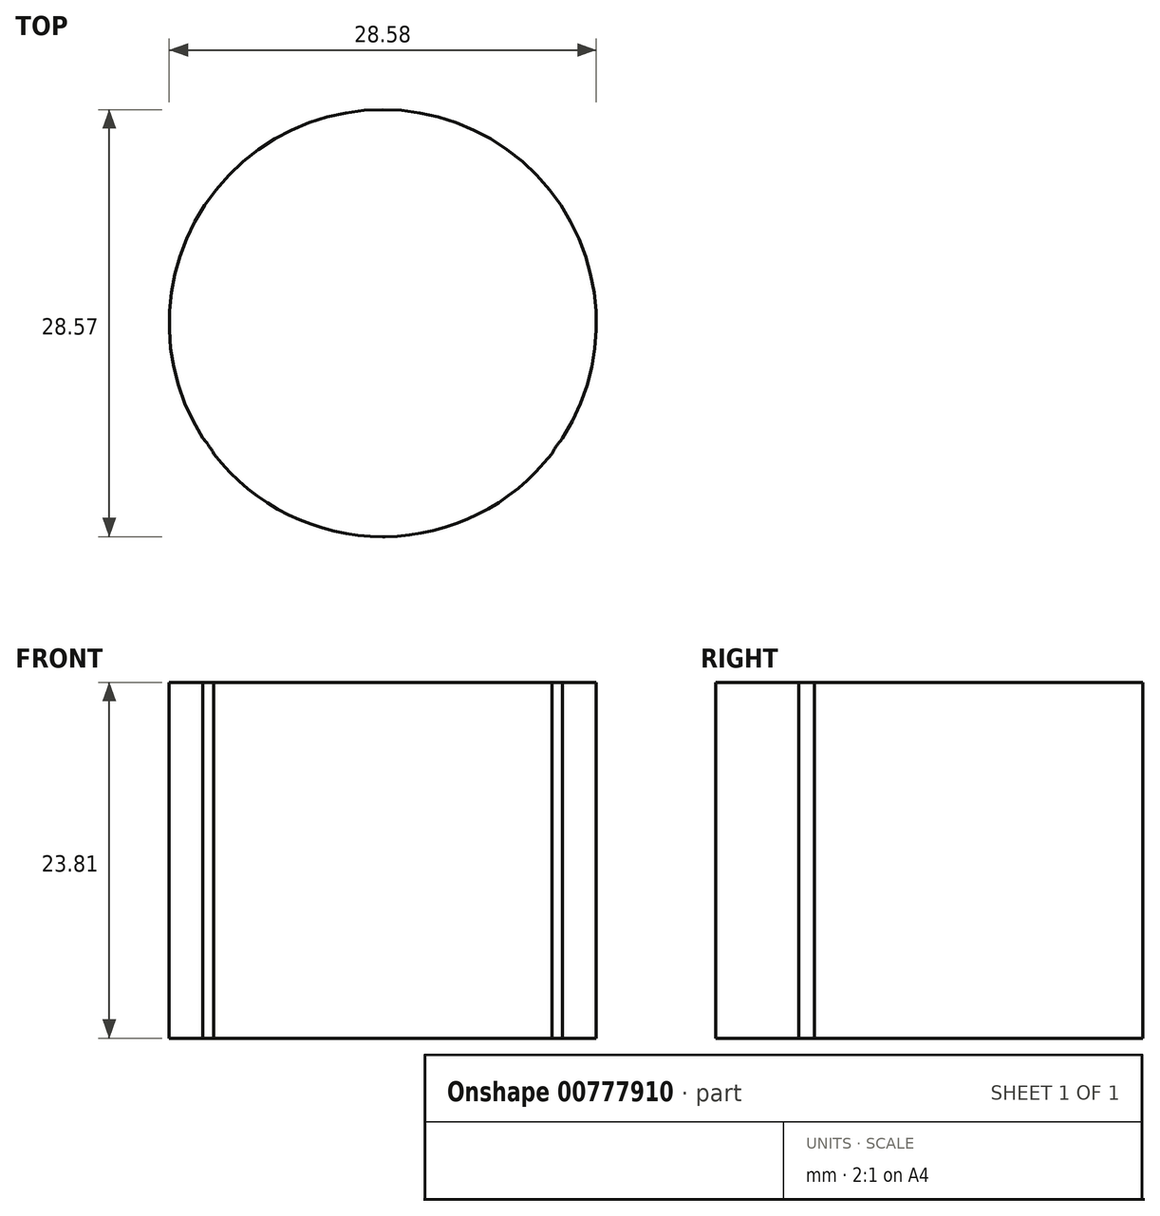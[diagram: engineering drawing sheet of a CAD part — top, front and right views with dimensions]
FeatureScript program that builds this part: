
annotation { "Feature Type Name" : "Feature", "Feature Type Description" : "" }
export const myFeature = defineFeature(function(context is Context, id is Id, definition is map)
    precondition{}
    {
        {
            var Q0;
            Q0=qCreatedBy(makeId("Top.planeOp"),FACE);
            var sketch = newSketch(context, id + "F0", { "sketchPlane" : qUnion([Q0])});
            skCircle(sketch, "E0", {"center": v(0, 0) * mm, "radius": 33.34 * mm});
            skLineSegment(sketch, "E1", {"start": v(0, 33.34) * mm, "end": v(0, 115.89) * mm});
            skLineSegment(sketch, "E2", {"start": v(0, 115.89) * mm, "end": v(0, 144.46) * mm});
            skLineSegment(sketch, "E3", {"start": v(0, 115.89) * mm, "end": v(0, 130.18) * mm});
            skCircle(sketch, "E4", {"center": v(0, 130.18) * mm, "radius": 14.29 * mm});
            skLineSegment(sketch, "E5", {"start": v(0, 115.89) * mm, "end": v(0, 109.54) * mm});
            skLineSegment(sketch, "E6", {"start": v(0, 109.54) * mm, "end": v(8.73, 109.54) * mm});
            skLineSegment(sketch, "E7", {"start": v(8.73, 109.54) * mm, "end": v(0, 109.54) * mm});
            skLineSegment(sketch, "E8", {"start": v(0, 109.54) * mm, "end": v(-8.73, 109.54) * mm});
            skFitSpline(sketch, "E9", {"points": [v(8.73, 109.54) * mm, v(9.35, 115.94) * mm, v(11.31, 121.45) * mm, v(12.03, 122.47) * mm], "startDerivative": vector(0.44, 14.94) * mm, "endDerivative": vector(3.59, 4.17) * mm});
            skLineSegment(sketch, "E10", {"start": v(8.8, 111.62) * mm, "end": v(0, 111.62) * mm});
            skLineSegment(sketch, "E11", {"start": v(0, 111.62) * mm, "end": v(-8.79, 111.62) * mm});
            skLineSegment(sketch, "E12", {"start": v(9.35, 115.94) * mm, "end": v(0, 115.89) * mm});
            skLineSegment(sketch, "E13", {"start": v(-9.35, 115.89) * mm, "end": v(0, 115.89) * mm});
            skLineSegment(sketch, "E14", {"start": v(11.31, 121.45) * mm, "end": v(0, 121.45) * mm});
            skLineSegment(sketch, "E15", {"start": v(0, 121.45) * mm, "end": v(-11.31, 121.45) * mm});
            skLineSegment(sketch, "E16", {"start": v(12.03, 122.47) * mm, "end": v(0, 122.47) * mm});
            skLineSegment(sketch, "E17", {"start": v(0, 122.47) * mm, "end": v(-12.03, 122.47) * mm});
            skFitSpline(sketch, "E18", {"points": [v(-8.79, 111.62) * mm, v(-9.35, 115.89) * mm, v(-11.31, 121.45) * mm, v(-12.03, 122.47) * mm], "startDerivative": vector(-0.67, 10.56) * mm, "endDerivative": vector(-3.31, 3.73) * mm});
            skFitSpline(sketch, "E19", {"points": [v(-8.73, 109.54) * mm, v(-8.79, 111.62) * mm], "startDerivative": vector(-0.06, 2.08) * mm, "endDerivative": vector(-0.06, 2.08) * mm});
            skLineSegment(sketch, "E20", {"start": v(0, 33.34) * mm, "end": v(0, 63.5) * mm});
            skLineSegment(sketch, "E21", {"start": v(0, 63.5) * mm, "end": v(9.52, 63.5) * mm});
            skLineSegment(sketch, "E22", {"start": v(0, 63.5) * mm, "end": v(-9.53, 63.5) * mm});
            skFitSpline(sketch, "E23", {"points": [v(9.52, 63.5) * mm, v(8.73, 109.54) * mm], "startDerivative": vector(-0.8, 39.69) * mm, "endDerivative": vector(-0.8, 39.69) * mm});
            skFitSpline(sketch, "E24", {"points": [v(-9.53, 63.5) * mm, v(-8.75, 110.23) * mm], "startDerivative": vector(0.78, 40.38) * mm, "endDerivative": vector(0.78, 40.38) * mm});
            skLineSegment(sketch, "E25", {"start": v(0, 33.34) * mm, "end": v(0, 57.15) * mm});
            skLineSegment(sketch, "E26", {"start": v(0, 57.15) * mm, "end": v(11.11, 57.15) * mm});
            skLineSegment(sketch, "E27", {"start": v(0, 57.15) * mm, "end": v(-11.11, 57.15) * mm});
            skLineSegment(sketch, "E28", {"start": v(0, 33.34) * mm, "end": v(0, 49.21) * mm});
            skLineSegment(sketch, "E29", {"start": v(0, 49.21) * mm, "end": v(14.29, 49.21) * mm});
            skLineSegment(sketch, "E30", {"start": v(0, 49.21) * mm, "end": v(-14.29, 49.21) * mm});
            skCircle(sketch, "E31", {"center": v(0, 0) * mm, "radius": 30.96 * mm});
            skLineSegment(sketch, "E32", {"start": v(0, 33.34) * mm, "end": v(0, 42.86) * mm});
            skLineSegment(sketch, "E33", {"start": v(0, 42.86) * mm, "end": v(0, 33.34) * mm});
            skLineSegment(sketch, "E34", {"start": v(0, 42.86) * mm, "end": v(16.67, 42.86) * mm});
            skLineSegment(sketch, "E35", {"start": v(0, 42.86) * mm, "end": v(-16.66, 42.86) * mm});
            skLineSegment(sketch, "E36", {"start": v(0, 33.34) * mm, "end": v(0, 0) * mm});
            skLineSegment(sketch, "E37", {"start": v(0, 0) * mm, "end": v(33.34, 0) * mm});
            skLineSegment(sketch, "E38", {"start": v(33.34, 0) * mm, "end": v(33.34, 25.4) * mm});
            skLineSegment(sketch, "E39", {"start": v(33.34, 25.4) * mm, "end": v(-21.6, 25.4) * mm});
            skLineSegment(sketch, "E40", {"start": v(33.34, 25.4) * mm, "end": v(21.6, 25.4) * mm});
            skFitSpline(sketch, "E41", {"points": [v(9.52, 63.5) * mm, v(11.11, 57.15) * mm, v(14.29, 49.21) * mm, v(16.67, 42.86) * mm, v(20.38, 33.37) * mm, v(21.6, 25.4) * mm], "startDerivative": vector(6.83, -33.8) * mm, "endDerivative": vector(3.07, -38.36) * mm});
            skLineSegment(sketch, "E42", {"start": v(0, 33.34) * mm, "end": v(-20.37, 33.34) * mm});
            skFitSpline(sketch, "E43", {"points": [v(-9.53, 63.5) * mm, v(-11.11, 57.15) * mm, v(-14.29, 49.21) * mm, v(-16.66, 42.86) * mm, v(-20.37, 33.34) * mm, v(-21.6, 25.4) * mm], "startDerivative": vector(-6.82, -33.8) * mm, "endDerivative": vector(-3.13, -38.24) * mm});
            skLineSegment(sketch, "E44", {"start": v(21.6, 25.4) * mm, "end": v(39.69, 25.4) * mm});
            skLineSegment(sketch, "E45", {"start": v(39.69, 25.4) * mm, "end": v(39.69, 0) * mm});
            skLineSegment(sketch, "E46", {"start": v(39.69, 0) * mm, "end": v(33.34, 0) * mm});
            skLineSegment(sketch, "E47", {"start": v(-21.6, 25.4) * mm, "end": v(-39.69, 25.4) * mm});
            skLineSegment(sketch, "E48", {"start": v(-39.69, 25.4) * mm, "end": v(-39.69, 0) * mm});
            skLineSegment(sketch, "E49", {"start": v(-39.69, 0) * mm, "end": v(-33.34, 0) * mm});
            skSolve(sketch);
        }
        {
            var Q0;
            {var subQ0=sQuery(id+"F0.wireOp",EDGE,"E2");Q0=makeQuery(id+"F0.imprint","IMPRINT",FACE,{"disambiguationData":[TD([[makeQuery(id+"F0.imprint","IMPRINT",EDGE,{"derivedFrom":subQ0}),1.0]])]});}
            var Q1;
            {var subQ0=sQuery(id+"F0.wireOp",EDGE,"E2");Q1=makeQuery(id+"F0.imprint","IMPRINT",FACE,{"disambiguationData":[TD([[makeQuery(id+"F0.imprint","IMPRINT",EDGE,{"derivedFrom":subQ0}),-1.0]])]});}
            var Q2;
            {var subQ0=sQuery(id+"F0.wireOp",EDGE,"E14");Q2=makeQuery(id+"F0.imprint","IMPRINT",FACE,{"disambiguationData":[TD([[makeQuery(id+"F0.imprint","IMPRINT",EDGE,{"derivedFrom":subQ0}),-1.0]])]});}
            var Q3;
            {var subQ3=sQuery(id+"F0.wireOp",EDGE,"E14");Q3=makeQuery(id+"F0.imprint","IMPRINT",FACE,{"disambiguationData":[TD([[makeQuery(id+"F0.imprint","IMPRINT",EDGE,{"derivedFrom":subQ3}),1.0]])]});}
            var Q4;
            {var subQ0=sQuery(id+"F0.wireOp",EDGE,"E15");Q4=makeQuery(id+"F0.imprint","IMPRINT",FACE,{"disambiguationData":[TD([[makeQuery(id+"F0.imprint","IMPRINT",EDGE,{"derivedFrom":subQ0}),-1.0]])]});}
            var Q5;
            {var subQ3=sQuery(id+"F0.wireOp",EDGE,"E15");Q5=makeQuery(id+"F0.imprint","IMPRINT",FACE,{"disambiguationData":[TD([[makeQuery(id+"F0.imprint","IMPRINT",EDGE,{"derivedFrom":subQ3}),1.0]])]});}
            extrude(context, id + "F1", {"entities" : qUnion([Q0, Q1, Q2, Q3, Q4, Q5]), "depth" : 11.1 * mm, "offsetDistance" : 25.4 * mm, "hasSecondDirection" : true, "secondDirectionOppositeDirection" : true, "secondDirectionDepth" : 12.7 * mm});
        }
    });
